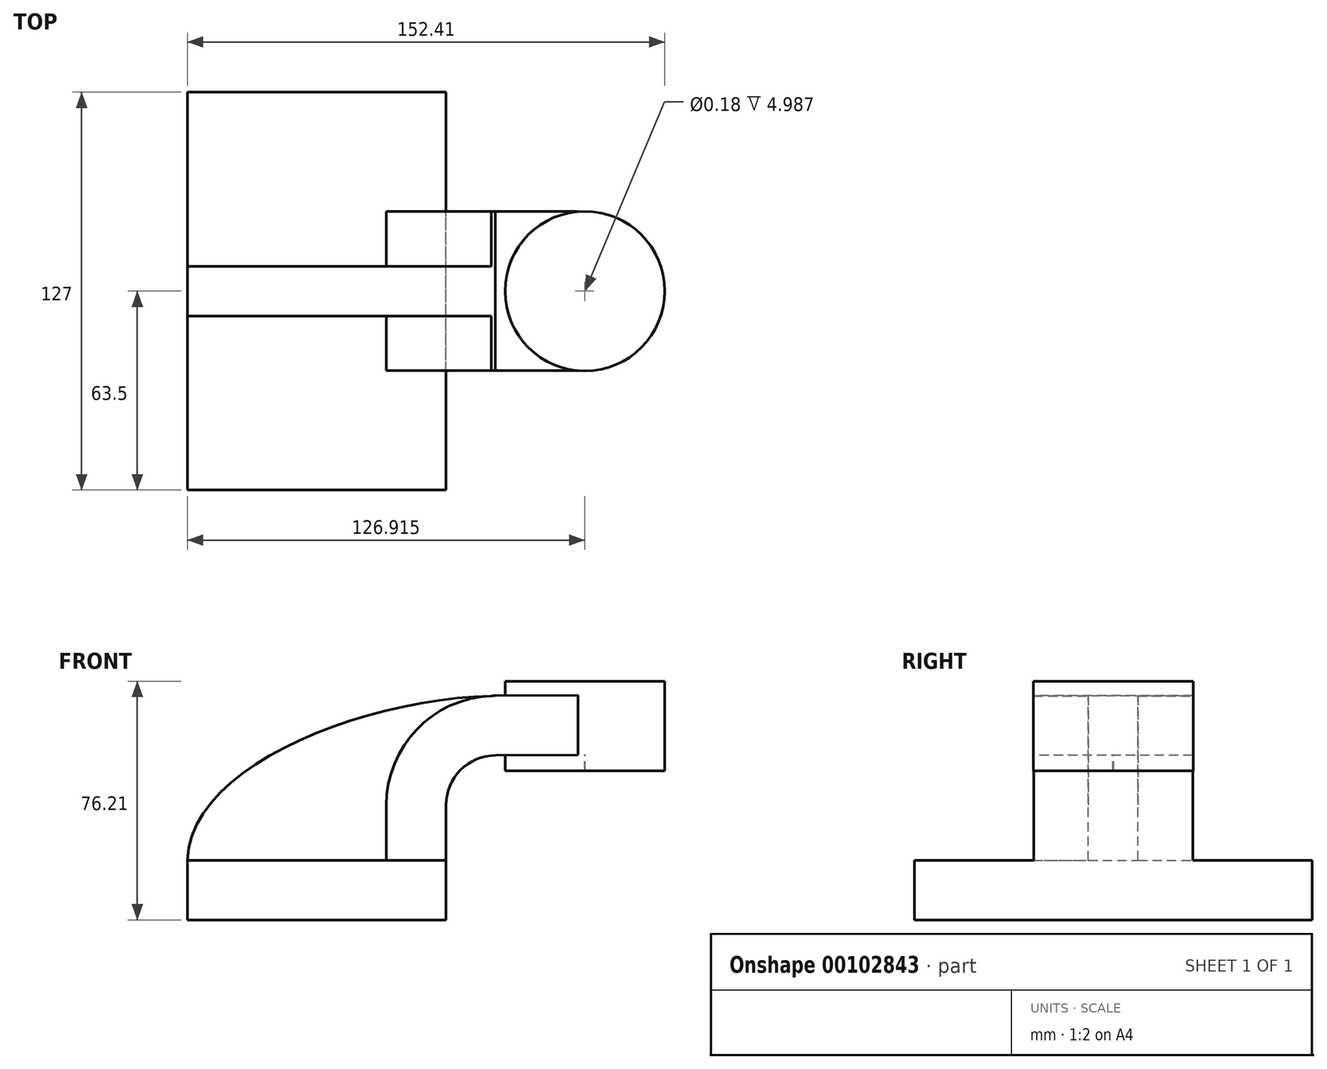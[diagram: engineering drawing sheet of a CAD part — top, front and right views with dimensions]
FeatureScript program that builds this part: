
annotation { "Feature Type Name" : "Feature", "Feature Type Description" : "" }
export const myFeature = defineFeature(function(context is Context, id is Id, definition is map)
    precondition{}
    {
        {
            var Q0;
            Q0=qCreatedBy(makeId("Front.planeOp"),FACE);
            var sketch = newSketch(context, id + "F0", { "sketchPlane" : qUnion([Q0])});
            skLineSegment(sketch, "E0.bottom", {"start": v(-41.28, -9.53) * mm, "end": v(41.28, -9.53) * mm});
            skLineSegment(sketch, "E0.top", {"start": v(-41.28, 9.53) * mm, "end": v(41.28, 9.53) * mm});
            skLineSegment(sketch, "E0.left", {"start": v(-41.28, -9.53) * mm, "end": v(-41.28, 9.53) * mm});
            skLineSegment(sketch, "E0.right", {"start": v(41.28, -9.53) * mm, "end": v(41.28, 9.53) * mm});
            skPoint(sketch, "E0.middle", {"position": v(0, 0) * mm});
            skLineSegment(sketch, "E1", {"start": v(41.27, 9.53) * mm, "end": v(41.27, 27.08) * mm});
            skArc(sketch, "E2", {"start": v(41.27, 27.08) * mm, "mid": v(45.9, 38.27) * mm, "end": v(57.07, 42.95) * mm});
            skLineSegment(sketch, "E3.bottom", {"start": v(111.12, 66.67) * mm, "end": v(60.32, 66.67) * mm});
            skLineSegment(sketch, "E3.top", {"start": v(111.12, 38.1) * mm, "end": v(60.32, 38.1) * mm});
            skLineSegment(sketch, "E3.left", {"start": v(111.12, 66.67) * mm, "end": v(111.12, 38.1) * mm});
            skLineSegment(sketch, "E3.right", {"start": v(60.32, 66.67) * mm, "end": v(60.32, 38.1) * mm});
            skPoint(sketch, "E3.middle", {"position": v(85.72, 52.39) * mm});
            skLineSegment(sketch, "E4", {"start": v(57.07, 42.95) * mm, "end": v(85.72, 43.09) * mm});
            skPoint(sketch, "E4.endSnap0", {"position": v(85.72, 38.1) * mm});
            skLineSegment(sketch, "E5.0", {"start": v(56.98, 62) * mm, "end": v(85.63, 62.14) * mm});
            skArc(sketch, "E5.1", {"start": v(22.22, 27.08) * mm, "mid": v(32.4, 51.71) * mm, "end": v(56.98, 62) * mm});
            skLineSegment(sketch, "E5.2", {"start": v(22.22, 9.53) * mm, "end": v(22.22, 27.08) * mm});
            skFitSpline(sketch, "E6", {"points": [v(-41.28, 9.53) * mm, v(56.98, 62) * mm], "startDerivative": vector(1.7, 91.44) * mm, "endDerivative": vector(122.94, 2.18) * mm});
            skLineSegment(sketch, "E7", {"start": v(85.72, 38.1) * mm, "end": v(85.72, 43.09) * mm});
            skLineSegment(sketch, "E8", {"start": v(85.72, 52.39) * mm, "end": v(85.72, 43.09) * mm});
            skLineSegment(sketch, "E9", {"start": v(85.72, 52.39) * mm, "end": v(85.63, 62.14) * mm});
            skLineSegment(sketch, "E10", {"start": v(85.63, 66.67) * mm, "end": v(85.63, 62.14) * mm});
            skPoint(sketch, "E10.startSnap0", {"position": v(85.72, 66.67) * mm});
            skSolve(sketch);
        }
        {
            var Q0;
            Q0=makeQuery(id+"F0.imprint","IMPRINT",FACE,{"disambiguationData":[TD([[makeQuery(id+"F0.imprint","IMPRINT",EDGE,{"derivedFrom":sQuery(id+"F0.wireOp",EDGE,"E0.bottom")}),1.0]])]});
            extrude(context, id + "F1", {"entities" : qUnion([Q0]), "endBound" : BoundingType.SYMMETRIC, "depth" : 127 * mm});
        }
        {
            var Q0;
            {var subQ9=sQuery(id+"F0.wireOp",EDGE,"E1");Q0=makeQuery(id+"F0.imprint","IMPRINT",FACE,{"disambiguationData":[TD([[makeQuery(id+"F0.imprint","IMPRINT",EDGE,{"derivedFrom":subQ9}),1.0]])]});}
            var Q1;
            {var subQ0=sQuery(id+"F0.wireOp",EDGE,"E8");Q1=makeQuery(id+"F0.imprint","IMPRINT",FACE,{"disambiguationData":[TD([[makeQuery(id+"F0.imprint","IMPRINT",EDGE,{"derivedFrom":subQ0}),-1.0]])]});}
            extrude(context, id + "F2", {"entities" : qUnion([Q0, Q1]), "operationType" : NewBodyOperationType.ADD, "endBound" : BoundingType.SYMMETRIC, "depth" : 50.8 * mm});
        }
        {
            var Q0;
            {var subQ3=sQuery(id+"F0.wireOp",EDGE,"E5.2");Q0=makeQuery(id+"F0.imprint","IMPRINT",FACE,{"disambiguationData":[TD([[makeQuery(id+"F0.imprint","IMPRINT",EDGE,{"derivedFrom":subQ3}),1.0]])]});}
            extrude(context, id + "F3", {"entities" : qUnion([Q0]), "operationType" : NewBodyOperationType.ADD, "endBound" : BoundingType.SYMMETRIC, "depth" : 15.88 * mm});
        }
        {
            var Q0;
            {var subQ1=sQuery(id+"F0.wireOp",EDGE,"E3.left");Q0=makeQuery(id+"F0.imprint","IMPRINT",FACE,{"disambiguationData":[TD([[makeQuery(id+"F0.imprint","IMPRINT",EDGE,{"derivedFrom":subQ1}),-1.0]])]});}
            var Q1;
            Q1=sQuery(id+"F0.wireOp",EDGE,"E10");
            revolve(context, id + "F4", {"operationType" : NewBodyOperationType.ADD, "entities" : qUnion([Q0]), "axis" : qUnion([Q1]), "revolveType" : RevolveType.FULL});
        }
    });
